# Revit family: SG
name_source: partatom
category: Lighting Fixtures
units: mm (PartAtom-declared; Revit-internal decimal feet)

## family parameters
Always vertical = Yes
Cut with Voids When Loaded = No
Host = Wall
Light Source = No
OmniClass Number = 23.80.70.14.14
OmniClass Title = Exterior Floodlights
Part Type = Normal
Room Calculation Point = No
Round Connector Dimension = Use Diameter
Shared = No

## types (5) — shared parameters
Apparent Load = 20 VA
Assembly Code = D5020200
Description = Perimeter wall or flood illumination
Glass = White Glass
Lamp = LED
Load Classification = Lighting
Manufacturer = EXO
Model = SG Sling
Power Factor = 1
URL = https://www.currentlighting.com
Voltage = 120 V
Wattage Comments = 20, 30, 50,& 80W
zero-valued in all types: Default Elevation

## per-type parameters (varying)
| type | Box Finish | Photometric Web | Product Option |
| SG-BL | Textured Black | Web SG : SG2-50-3K-PCU | Sling Series : SG2 |
| SG-DB | Textured Dark Bronze | Web SG : SG1-20-PCU | Sling Series : SG2 |
| SG-WH | Textured White | Web SG : SG1-20-PCU | Sling Series : SG1 |
| SG-GYS | Smooth Gray | Web SG : SG1-20-PCU | Sling Series : SG2 |
| SG-PS | Platinum | Web SG : SG1-20-PCU | Sling Series : SG1 |

## geometry (parser evidence)
native form markers: Blend x12, Sweep x7
no freeform markers — native parametric forms only
